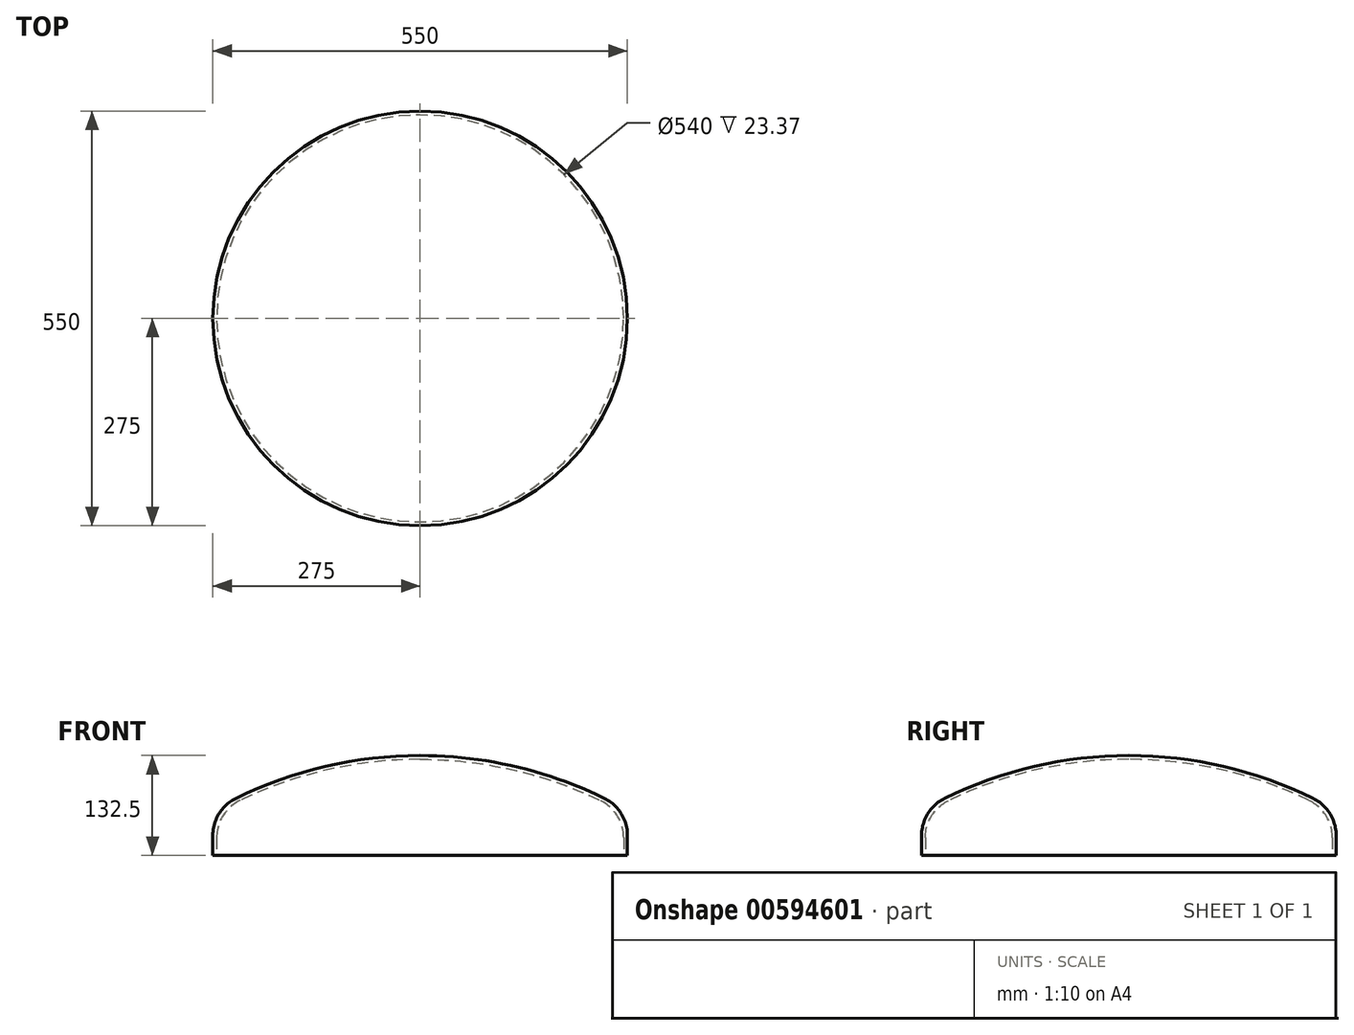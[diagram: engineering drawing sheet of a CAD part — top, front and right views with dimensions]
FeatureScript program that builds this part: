
annotation { "Feature Type Name" : "Feature", "Feature Type Description" : "" }
export const myFeature = defineFeature(function(context is Context, id is Id, definition is map)
    precondition{}
    {
        {
            var Q0;
            Q0=qCreatedBy(makeId("Front.planeOp"),FACE);
            var sketch = newSketch(context, id + "F0", { "sketchPlane" : qUnion([Q0])});
            skArc(sketch, "E0", {"start": v(-275, 476.31) * mm, "mid": v(0, -550) * mm, "end": v(275, 476.31) * mm});
            skLineSegment(sketch, "E1", {"start": v(0, 0) * mm, "end": v(721.01, 0) * mm});
            skLineSegment(sketch, "E2", {"start": v(275, 482.08) * mm, "end": v(275, 0) * mm});
            skCircle(sketch, "E3", {"center": v(0, 0) * mm, "radius": 555 * mm});
            skLineSegment(sketch, "E4", {"start": v(270, 479.17) * mm, "end": v(270, 0) * mm});
            skLineSegment(sketch, "E5", {"start": v(0, 0) * mm, "end": v(0, 190.02) * mm});
            skLineSegment(sketch, "E6.MirrorCS", {"start": v(540, 0) * mm, "end": v(540, 190.02) * mm});
            skLineSegment(sketch, "E7.MirrorCS", {"start": v(-270, 479.17) * mm, "end": v(-270, 0) * mm});
            skLineSegment(sketch, "E8.MirrorCS", {"start": v(-275, 482.08) * mm, "end": v(-275, 0) * mm});
            skLineSegment(sketch, "E9", {"start": v(270, 422.5) * mm, "end": v(275, 422.5) * mm});
            skArc(sketch, "E10.trimOffspring", {"start": v(270, 479.17) * mm, "mid": v(0, 550) * mm, "end": v(-270, 479.17) * mm});
            skLineSegment(sketch, "E11.trimOffspring", {"start": v(-275, 422.5) * mm, "end": v(-270, 422.5) * mm});
            skLineSegment(sketch, "E12", {"start": v(0, 0) * mm, "end": v(0, 678.68) * mm});
            skSolve(sketch);
        }
        {
            var Q0;
            {var subQ3=sQuery(id+"F0.wireOp",EDGE,"E9");Q0=makeQuery(id+"F0.imprint","IMPRINT",FACE,{"disambiguationData":[TD([[makeQuery(id+"F0.imprint","IMPRINT",EDGE,{"derivedFrom":subQ3}),1.0]])]});}
            var Q1;
            Q1=sQuery(id+"F0.wireOp",EDGE,"E12");
            revolve(context, id + "F1", {"entities" : qUnion([Q0]), "axis" : qUnion([Q1]), "revolveType" : RevolveType.FULL});
        }
        {
            var Q0;
            Q0=makeQuery(id+"F1.opRevolve","SWEPT_EDGE",EDGE,{"disambiguationData":[OSD([sQuery(id+"F0.wireOp",EDGE,"E4"),sQuery(id+"F0.wireOp",EDGE,"E10.trimOffspring")])]});
            fillet(context, id + "F2", {"entities" : qUnion([Q0]), "radius" : (0.1 * 550) * mm, "tangentPropagation" : true, "allowEdgeOverflow" : false});
        }
        {
            var Q0;
            Q0=makeQuery(id+"F1.opRevolve","SWEPT_EDGE",EDGE,{"disambiguationData":[OSD([sQuery(id+"F0.wireOp",EDGE,"E2"),sQuery(id+"F0.wireOp",EDGE,"E3")])]});
            fillet(context, id + "F3", {"entities" : qUnion([Q0]), "radius" : (0.1 * 550) * mm, "tangentPropagation" : true, "allowEdgeOverflow" : false});
        }
    });
